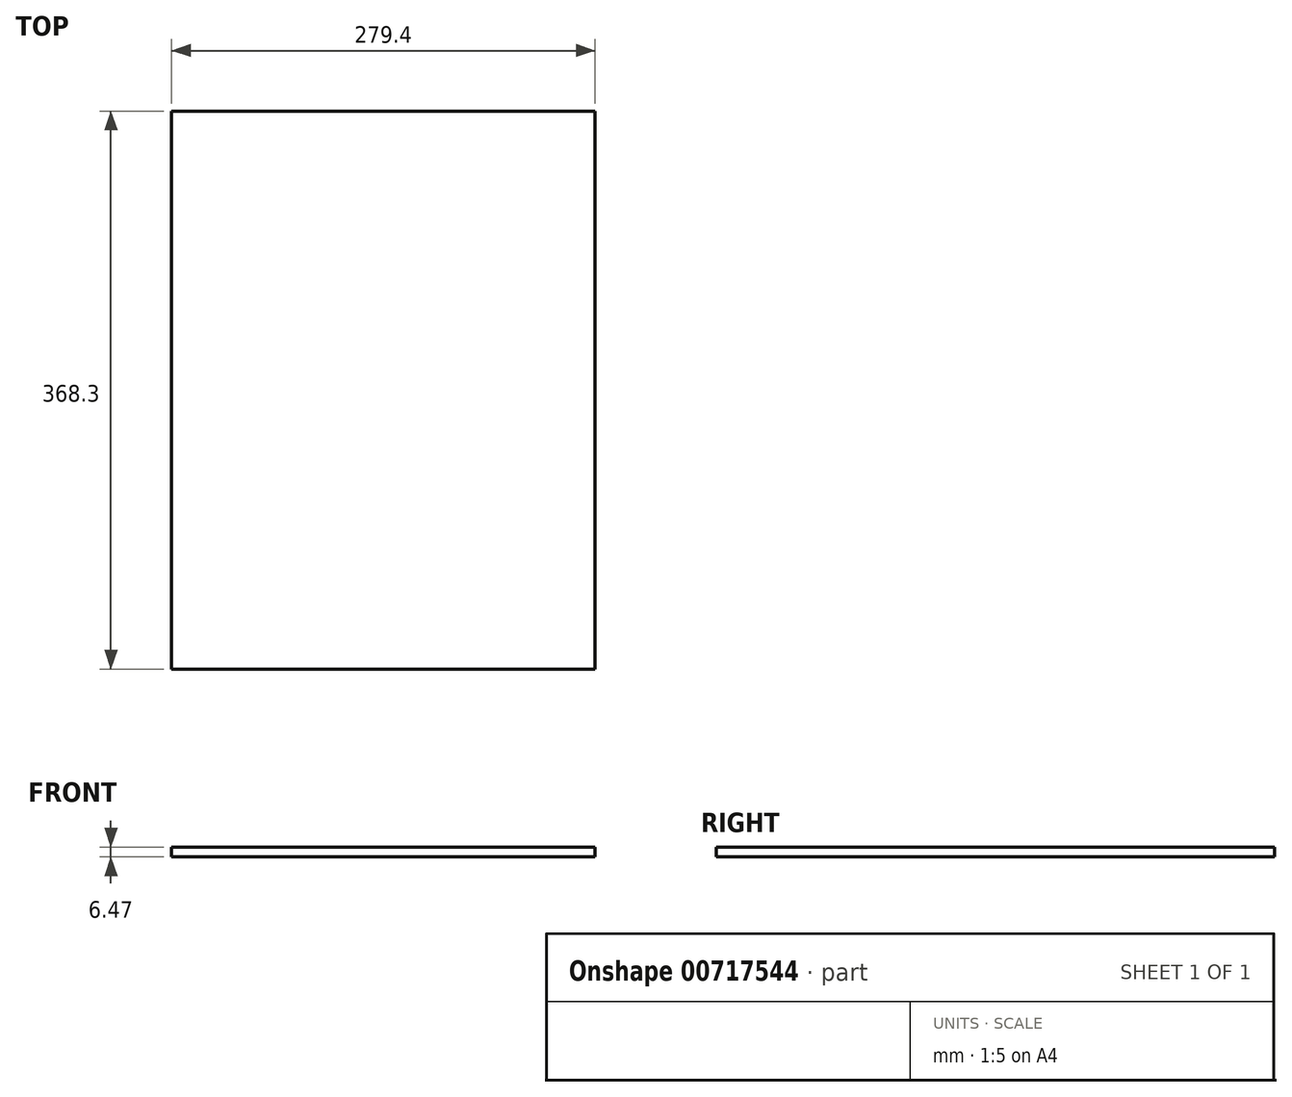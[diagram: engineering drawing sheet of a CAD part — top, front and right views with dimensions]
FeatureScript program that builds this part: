
annotation { "Feature Type Name" : "Feature", "Feature Type Description" : "" }
export const myFeature = defineFeature(function(context is Context, id is Id, definition is map)
    precondition{}
    {
        {
            var Q0;
            Q0=qCreatedBy(makeId("Front.planeOp"),FACE);
            var sketch = newSketch(context, id + "F0", { "sketchPlane" : qUnion([Q0])});
            skLineSegment(sketch, "E0.bottom", {"start": v(-190.7, 24.6) * mm, "end": v(88.7, 24.6) * mm});
            skLineSegment(sketch, "E0.top", {"start": v(-190.7, 31.07) * mm, "end": v(88.7, 31.07) * mm});
            skLineSegment(sketch, "E0.left", {"start": v(-190.7, 24.6) * mm, "end": v(-190.7, 31.07) * mm});
            skLineSegment(sketch, "E0.right", {"start": v(88.7, 24.6) * mm, "end": v(88.7, 31.07) * mm});
            skSolve(sketch);
        }
        {
            var Q0;
            Q0=makeQuery(id+"F0.imprint","IMPRINT",FACE,{"disambiguationData":[TD([[makeQuery(id+"F0.imprint","IMPRINT",EDGE,{"derivedFrom":sQuery(id+"F0.wireOp",EDGE,"E0.bottom")}),1.0]])]});
            extrude(context, id + "F1", {"entities" : qUnion([Q0]), "depth" : 368.3 * mm, "offsetDistance" : 25.4 * mm});
        }
    });
